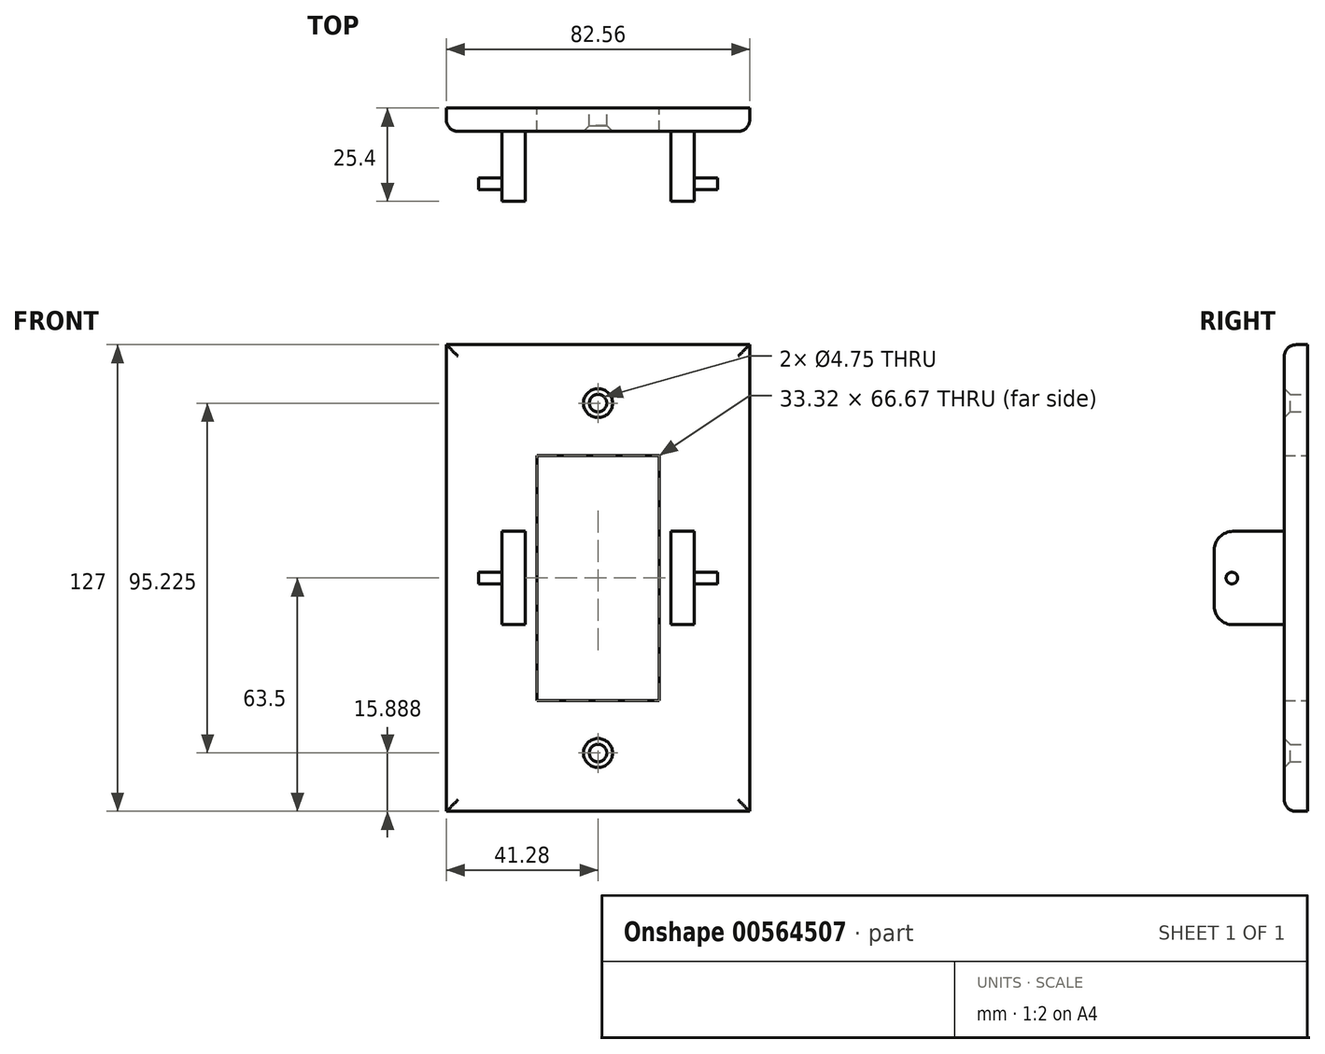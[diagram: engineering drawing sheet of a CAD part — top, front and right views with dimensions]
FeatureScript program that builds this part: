
annotation { "Feature Type Name" : "Feature", "Feature Type Description" : "" }
export const myFeature = defineFeature(function(context is Context, id is Id, definition is map)
    precondition{}
    {
        {
            var Q0;
            Q0=qCreatedBy(makeId("Front.planeOp"),FACE);
            var sketch = newSketch(context, id + "F0", { "sketchPlane" : qUnion([Q0])});
            skLineSegment(sketch, "E0.bottom", {"start": v(41.28, -63.5) * mm, "end": v(-41.28, -63.5) * mm});
            skLineSegment(sketch, "E0.top", {"start": v(41.27, 63.5) * mm, "end": v(-41.28, 63.5) * mm});
            skLineSegment(sketch, "E0.left", {"start": v(41.28, -63.5) * mm, "end": v(41.27, 63.5) * mm});
            skLineSegment(sketch, "E0.right", {"start": v(-41.28, -63.5) * mm, "end": v(-41.28, 63.5) * mm});
            skPoint(sketch, "E0.middle", {"position": v(0, 0) * mm});
            skLineSegment(sketch, "E1.bottom", {"start": v(16.66, -33.34) * mm, "end": v(-16.66, -33.34) * mm});
            skLineSegment(sketch, "E1.top", {"start": v(16.66, 33.34) * mm, "end": v(-16.66, 33.34) * mm});
            skLineSegment(sketch, "E1.left", {"start": v(16.66, -33.34) * mm, "end": v(16.66, 33.34) * mm});
            skLineSegment(sketch, "E1.right", {"start": v(-16.66, -33.34) * mm, "end": v(-16.66, 33.34) * mm});
            skCircle(sketch, "E2", {"center": v(0, -47.61) * mm, "radius": 2.37 * mm});
            skCircle(sketch, "E3", {"center": v(0, 47.61) * mm, "radius": 2.37 * mm});
            skLineSegment(sketch, "E4.bottom", {"start": v(-19.84, -12.7) * mm, "end": v(-26.19, -12.7) * mm});
            skLineSegment(sketch, "E4.top", {"start": v(-19.84, 12.7) * mm, "end": v(-26.19, 12.7) * mm});
            skLineSegment(sketch, "E4.left", {"start": v(-19.84, -12.7) * mm, "end": v(-19.84, 12.7) * mm});
            skLineSegment(sketch, "E4.right", {"start": v(-26.19, -12.7) * mm, "end": v(-26.19, 12.7) * mm});
            skPoint(sketch, "E4.middle", {"position": v(-23.01, 0) * mm});
            skLineSegment(sketch, "E5.bottom", {"start": v(26.19, 12.7) * mm, "end": v(19.84, 12.7) * mm});
            skLineSegment(sketch, "E5.top", {"start": v(26.19, -12.7) * mm, "end": v(19.84, -12.7) * mm});
            skLineSegment(sketch, "E5.left", {"start": v(26.19, 12.7) * mm, "end": v(26.19, -12.7) * mm});
            skLineSegment(sketch, "E5.right", {"start": v(19.84, 12.7) * mm, "end": v(19.84, -12.7) * mm});
            skPoint(sketch, "E5.middle", {"position": v(23.01, 0) * mm});
            skSolve(sketch);
        }
        {
            var Q0;
            Q0=makeQuery(id+"F0.imprint","IMPRINT",FACE,{"disambiguationData":[TD([[makeQuery(id+"F0.imprint","IMPRINT",EDGE,{"derivedFrom":sQuery(id+"F0.wireOp",EDGE,"E0.bottom")}),-1.0]])]});
            extrude(context, id + "F1", {"entities" : qUnion([Q0]), "depth" : 6.35 * mm, "offsetDistance" : 25.4 * mm});
        }
        {
            var Q0;
            Q0=makeQuery(id+"F1.opExtrude","CAP_EDGE",EDGE,{"disambiguationData":[OSD([sQuery(id+"F0.wireOp",EDGE,"E0.top")])],"isStart":false});
            var Q1;
            Q1=makeQuery(id+"F1.opExtrude","CAP_EDGE",EDGE,{"disambiguationData":[OSD([sQuery(id+"F0.wireOp",EDGE,"E0.left")])],"isStart":false});
            var Q2;
            Q2=makeQuery(id+"F1.opExtrude","CAP_EDGE",EDGE,{"disambiguationData":[OSD([sQuery(id+"F0.wireOp",EDGE,"E0.bottom")])],"isStart":false});
            var Q3;
            Q3=makeQuery(id+"F1.opExtrude","CAP_EDGE",EDGE,{"disambiguationData":[OSD([sQuery(id+"F0.wireOp",EDGE,"E0.right")])],"isStart":false});
            fillet(context, id + "F2", {"entities" : qUnion([Q0, Q1, Q2, Q3]), "radius" : 3.17 * mm, "tangentPropagation" : true, "allowEdgeOverflow" : false});
        }
        {
            var Q0;
            Q0=makeQuery(id+"F1.opExtrude","CAP_EDGE",EDGE,{"disambiguationData":[OSD([sQuery(id+"F0.wireOp",EDGE,"E3")])],"isStart":false});
            chamfer(context, id + "F3", {"entities" : qUnion([Q0]), "width" : 1.57 * mm, "tangentPropagation" : true});
        }
        {
            var Q0;
            Q0=makeQuery(id+"F1.opExtrude","CAP_EDGE",EDGE,{"disambiguationData":[OSD([sQuery(id+"F0.wireOp",EDGE,"E2")])],"isStart":false});
            chamfer(context, id + "F4", {"entities" : qUnion([Q0]), "width" : 1.57 * mm, "tangentPropagation" : true});
        }
        {
            var Q0;
            Q0=makeQuery(id+"F0.imprint","IMPRINT",FACE,{"disambiguationData":[TD([[makeQuery(id+"F0.imprint","IMPRINT",EDGE,{"derivedFrom":sQuery(id+"F0.wireOp",EDGE,"E4.bottom")}),-1.0]])]});
            extrude(context, id + "F5", {"entities" : qUnion([Q0]), "operationType" : NewBodyOperationType.ADD, "depth" : 25.4 * mm, "offsetDistance" : 25.4 * mm});
        }
        {
            var Q0;
            Q0=makeQuery(id+"F0.imprint","IMPRINT",FACE,{"disambiguationData":[TD([[makeQuery(id+"F0.imprint","IMPRINT",EDGE,{"derivedFrom":sQuery(id+"F0.wireOp",EDGE,"E5.bottom")}),1.0]])]});
            extrude(context, id + "F6", {"entities" : qUnion([Q0]), "operationType" : NewBodyOperationType.ADD, "depth" : 25.4 * mm, "offsetDistance" : 25.4 * mm});
        }
        {
            var Q0;
            Q0=makeQuery(id+"F5.opExtrude","CAP_EDGE",EDGE,{"disambiguationData":[OSD([sQuery(id+"F0.wireOp",EDGE,"E4.top")])],"isStart":false});
            fillet(context, id + "F7", {"entities" : qUnion([Q0]), "radius" : 5.08 * mm, "tangentPropagation" : true, "allowEdgeOverflow" : false});
        }
        {
            var Q0;
            Q0=makeQuery(id+"F6.opExtrude","CAP_EDGE",EDGE,{"disambiguationData":[OSD([sQuery(id+"F0.wireOp",EDGE,"E5.bottom")])],"isStart":false});
            var Q1;
            Q1=makeQuery(id+"F5.opExtrude","CAP_EDGE",EDGE,{"disambiguationData":[OSD([sQuery(id+"F0.wireOp",EDGE,"E4.bottom")])],"isStart":false});
            fillet(context, id + "F8", {"entities" : qUnion([Q0, Q1]), "radius" : 5.08 * mm, "tangentPropagation" : true, "allowEdgeOverflow" : false});
        }
        {
            var Q0;
            Q0=makeQuery(id+"F6.opExtrude","CAP_EDGE",EDGE,{"disambiguationData":[OSD([sQuery(id+"F0.wireOp",EDGE,"E5.top")])],"isStart":false});
            fillet(context, id + "F9", {"entities" : qUnion([Q0]), "radius" : 5.08 * mm, "tangentPropagation" : true, "allowEdgeOverflow" : false});
        }
        {
            var Q0;
            Q0=makeQuery(id+"F5.opExtrude","SWEPT_FACE",FACE,{"disambiguationData":[OSD([sQuery(id+"F0.wireOp",EDGE,"E4.right")])]});
            var sketch = newSketch(context, id + "F10", { "sketchPlane" : qUnion([Q0])});
            skCircle(sketch, "E6", {"center": v(20.64, 0) * mm, "radius": 1.59 * mm});
            skSolve(sketch);
        }
        {
            var Q0;
            Q0=makeQuery(id+"F10.imprint","IMPRINT",FACE,{"disambiguationData":[TD([[makeQuery(id+"F10.imprint","IMPRINT",EDGE,{"derivedFrom":sQuery(id+"F10.wireOp",EDGE,"E6")}),1.0]])]});
            extrude(context, id + "F11", {"entities" : qUnion([Q0]), "operationType" : NewBodyOperationType.ADD, "depth" : 6.35 * mm, "offsetDistance" : 25.4 * mm});
        }
        {
            var Q0;
            Q0=makeQuery(id+"F6.opExtrude","SWEPT_FACE",FACE,{"disambiguationData":[OSD([sQuery(id+"F0.wireOp",EDGE,"E5.left")])]});
            var sketch = newSketch(context, id + "F12", { "sketchPlane" : qUnion([Q0])});
            skCircle(sketch, "E7", {"center": v(-20.64, 0) * mm, "radius": 1.59 * mm});
            skSolve(sketch);
        }
        {
            var Q0;
            Q0=makeQuery(id+"F12.imprint","IMPRINT",FACE,{"disambiguationData":[TD([[makeQuery(id+"F12.imprint","IMPRINT",EDGE,{"derivedFrom":sQuery(id+"F12.wireOp",EDGE,"E7")}),1.0]])]});
            var Q1;
            Q1=sQuery(id+"F12.wireOp",EDGE,"E7");
            extrude(context, id + "F13", {"entities" : qUnion([Q0]), "operationType" : NewBodyOperationType.ADD, "surfaceEntities" : qUnion([Q1]), "depth" : 6.35 * mm, "offsetDistance" : 25.4 * mm});
        }
    });
